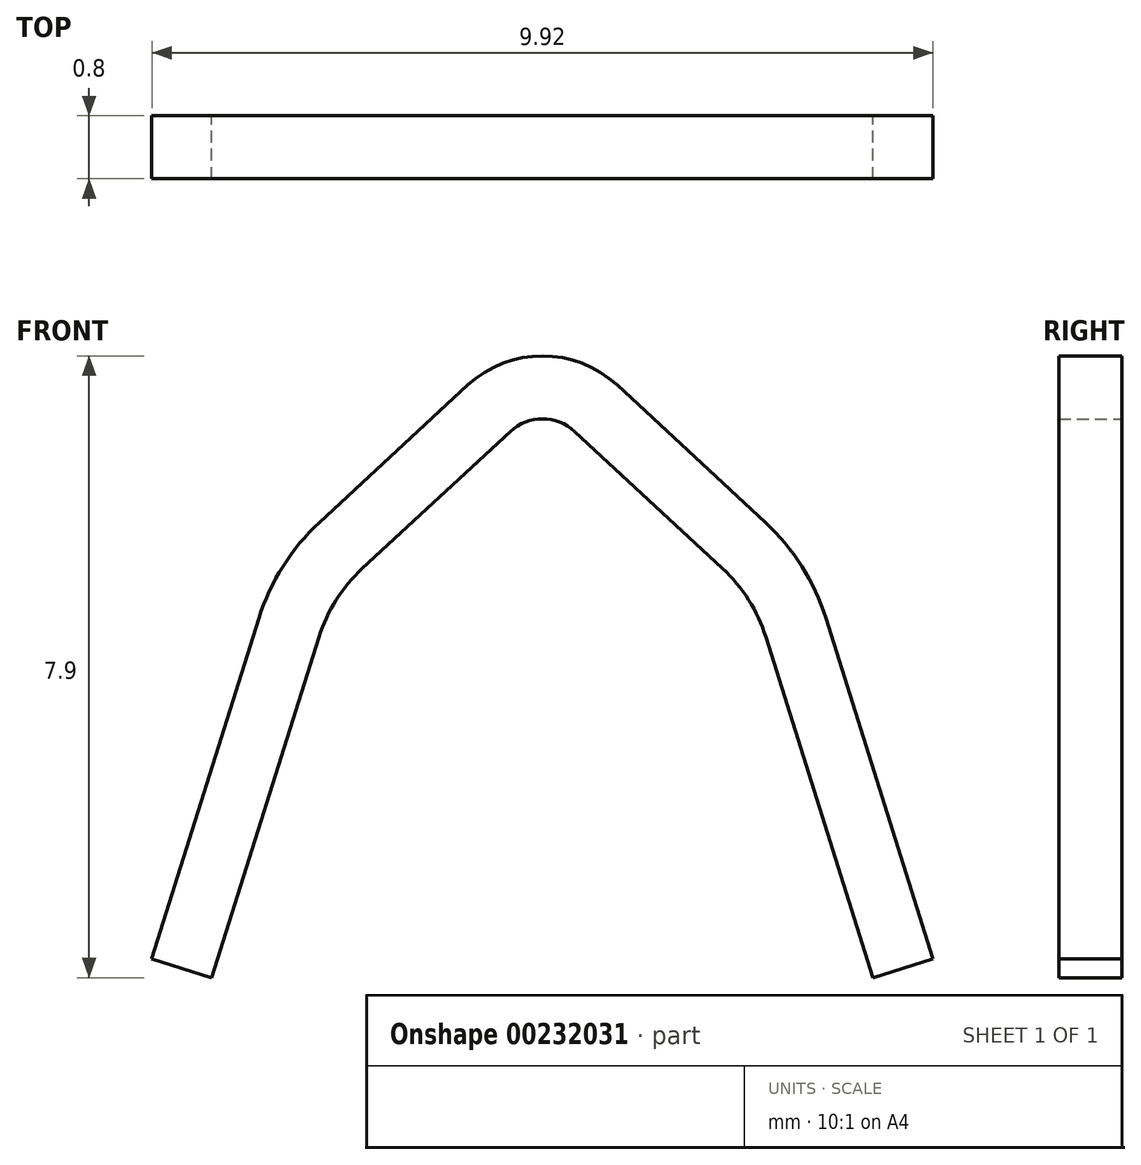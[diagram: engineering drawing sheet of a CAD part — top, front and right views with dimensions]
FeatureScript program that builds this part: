
annotation { "Feature Type Name" : "Feature", "Feature Type Description" : "" }
export const myFeature = defineFeature(function(context is Context, id is Id, definition is map)
    precondition{}
    {
        {
            var Q0;
            Q0=qCreatedBy(makeId("Front.planeOp"),FACE);
            var sketch = newSketch(context, id + "F0", { "sketchPlane" : qUnion([Q0])});
            skLineSegment(sketch, "E0", {"start": v(-4.2, 0) * mm, "end": v(-2.84, 4.33) * mm});
            skArc(sketch, "E1", {"start": v(-2.84, 4.33) * mm, "mid": v(-2.62, 4.8) * mm, "end": v(-2.29, 5.2) * mm});
            skLineSegment(sketch, "E2", {"start": v(-2.29, 5.2) * mm, "end": v(-0.4, 6.94) * mm});
            skArc(sketch, "E3", {"start": v(-0.4, 6.94) * mm, "mid": v(-0.22, 7.06) * mm, "end": v(0, 7.1) * mm});
            skLineSegment(sketch, "E4.MirrorCS", {"start": v(4.2, 0) * mm, "end": v(2.84, 4.33) * mm});
            skArc(sketch, "E5.MirrorCS", {"start": v(2.84, 4.33) * mm, "mid": v(2.62, 4.8) * mm, "end": v(2.29, 5.2) * mm});
            skLineSegment(sketch, "E6.MirrorCS", {"start": v(2.29, 5.2) * mm, "end": v(0.4, 6.94) * mm});
            skArc(sketch, "E7.MirrorCS", {"start": v(0.4, 6.94) * mm, "mid": v(0.22, 7.06) * mm, "end": v(0, 7.1) * mm});
            skLineSegment(sketch, "E8.0", {"start": v(4.96, 0.24) * mm, "end": v(3.6, 4.57) * mm});
            skArc(sketch, "E8.1", {"start": v(3.6, 4.57) * mm, "mid": v(3.3, 5.23) * mm, "end": v(2.83, 5.78) * mm});
            skLineSegment(sketch, "E8.2", {"start": v(2.83, 5.78) * mm, "end": v(0.95, 7.53) * mm});
            skArc(sketch, "E8.3", {"start": v(0.95, 7.53) * mm, "mid": v(0.51, 7.8) * mm, "end": v(0, 7.9) * mm});
            skLineSegment(sketch, "E8.4", {"start": v(-4.96, 0.24) * mm, "end": v(-3.6, 4.57) * mm});
            skArc(sketch, "E8.5", {"start": v(-3.6, 4.57) * mm, "mid": v(-3.3, 5.23) * mm, "end": v(-2.83, 5.78) * mm});
            skLineSegment(sketch, "E8.6", {"start": v(-2.83, 5.78) * mm, "end": v(-0.95, 7.53) * mm});
            skArc(sketch, "E8.7", {"start": v(-0.95, 7.53) * mm, "mid": v(-0.51, 7.8) * mm, "end": v(0, 7.9) * mm});
            skLineSegment(sketch, "E9", {"start": v(-4.96, 0.24) * mm, "end": v(-4.2, 0) * mm});
            skLineSegment(sketch, "E10", {"start": v(4.96, 0.24) * mm, "end": v(4.2, 0) * mm});
            skSolve(sketch);
        }
        {
            var Q0;
            Q0=makeQuery(id+"F0.imprint","IMPRINT",FACE,{"disambiguationData":[TD([[makeQuery(id+"F0.imprint","IMPRINT",EDGE,{"derivedFrom":sQuery(id+"F0.wireOp",EDGE,"E0")}),1.0]])]});
            extrude(context, id + "F1", {"entities" : qUnion([Q0]), "endBound" : BoundingType.SYMMETRIC, "depth" : 0.8 * mm});
        }
    });
